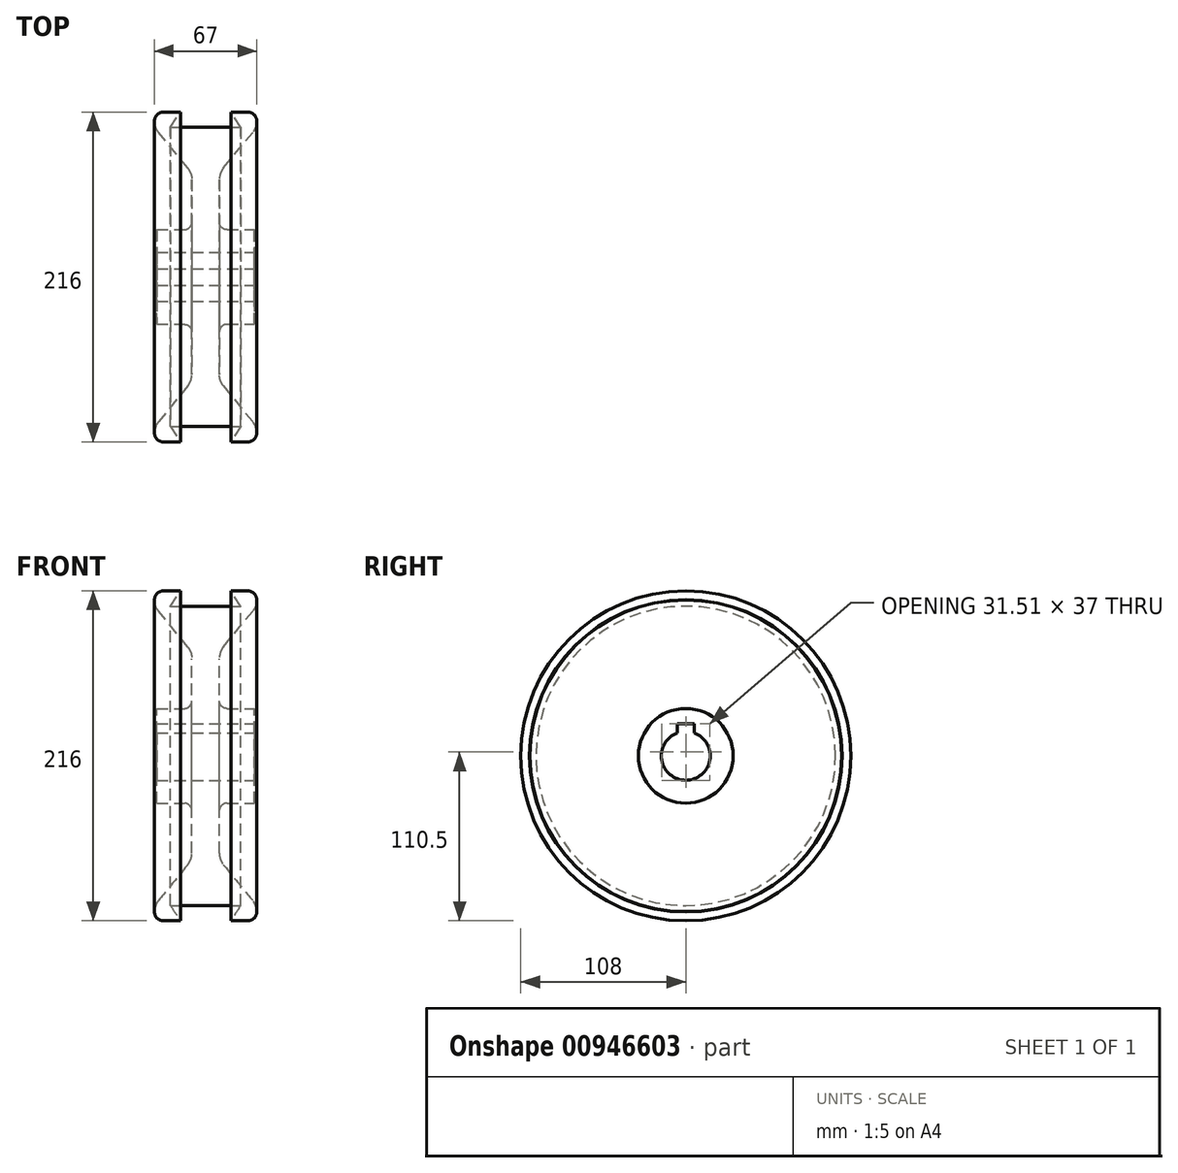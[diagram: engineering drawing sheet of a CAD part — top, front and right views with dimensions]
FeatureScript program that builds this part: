
annotation { "Feature Type Name" : "Feature", "Feature Type Description" : "" }
export const myFeature = defineFeature(function(context is Context, id is Id, definition is map)
    precondition{}
    {
        {
            var Q0;
            Q0=qCreatedBy(makeId("Front.planeOp"),FACE);
            var sketch = newSketch(context, id + "F0", { "sketchPlane" : qUnion([Q0])});
            skLineSegment(sketch, "E0", {"start": v(32, 0) * mm, "end": v(32, 31) * mm});
            skLineSegment(sketch, "E1", {"start": v(32, 31) * mm, "end": v(14, 31) * mm});
            skLineSegment(sketch, "E2", {"start": v(9, 36) * mm, "end": v(9, 63.72) * mm});
            skLineSegment(sketch, "E3", {"start": v(11.7, 71.31) * mm, "end": v(30.8, 94.69) * mm});
            skLineSegment(sketch, "E4", {"start": v(33.5, 102) * mm, "end": v(33.5, 102.28) * mm});
            skLineSegment(sketch, "E5", {"start": v(27.5, 108) * mm, "end": v(16.5, 108) * mm});
            skLineSegment(sketch, "E6", {"start": v(16.5, 108) * mm, "end": v(23, 98) * mm});
            skLineSegment(sketch, "E7", {"start": v(23, 98) * mm, "end": v(0, 98) * mm});
            skLineSegment(sketch, "E8", {"start": v(32, 0) * mm, "end": v(0, 0) * mm});
            skLineSegment(sketch, "E9.MirrorCS", {"start": v(-23, 98) * mm, "end": v(0, 98) * mm});
            skLineSegment(sketch, "E10.MirrorCS", {"start": v(-16.5, 108) * mm, "end": v(-23, 98) * mm});
            skLineSegment(sketch, "E11.MirrorCS", {"start": v(-27.5, 108) * mm, "end": v(-16.5, 108) * mm});
            skLineSegment(sketch, "E12.MirrorCS", {"start": v(-33.5, 102) * mm, "end": v(-33.5, 102.28) * mm});
            skLineSegment(sketch, "E13.MirrorCS", {"start": v(-11.7, 71.31) * mm, "end": v(-30.8, 94.69) * mm});
            skLineSegment(sketch, "E14.MirrorCS", {"start": v(-9, 36) * mm, "end": v(-9, 63.72) * mm});
            skLineSegment(sketch, "E15.MirrorCS", {"start": v(-32, 31) * mm, "end": v(-14, 31) * mm});
            skLineSegment(sketch, "E16.MirrorCS", {"start": v(-32, 0) * mm, "end": v(-32, 31) * mm});
            skLineSegment(sketch, "E17.MirrorCS", {"start": v(-32, 0) * mm, "end": v(0, 0) * mm});
            skPoint(sketch, "E18.visualSharp", {"position": v(-33.5, 108) * mm});
            skArc(sketch, "E18.filletArc", {"start": v(-27.5, 108) * mm, "mid": v(-31.74, 106.24) * mm, "end": v(-33.5, 102) * mm});
            skPoint(sketch, "E19.visualSharp", {"position": v(-33.5, 98) * mm});
            skArc(sketch, "E19.filletArc", {"start": v(-33.5, 102.28) * mm, "mid": v(-32.8, 98.25) * mm, "end": v(-30.8, 94.69) * mm});
            skPoint(sketch, "E20.visualSharp", {"position": v(33.5, 98) * mm});
            skArc(sketch, "E20.filletArc", {"start": v(30.8, 94.69) * mm, "mid": v(32.8, 98.25) * mm, "end": v(33.5, 102.28) * mm});
            skPoint(sketch, "E21.visualSharp", {"position": v(-9, 68) * mm});
            skArc(sketch, "E21.filletArc", {"start": v(-9, 63.72) * mm, "mid": v(-9.7, 67.75) * mm, "end": v(-11.7, 71.31) * mm});
            skPoint(sketch, "E22.visualSharp", {"position": v(9, 68) * mm});
            skArc(sketch, "E22.filletArc", {"start": v(11.7, 71.31) * mm, "mid": v(9.7, 67.75) * mm, "end": v(9, 63.72) * mm});
            skPoint(sketch, "E23.visualSharp", {"position": v(-9, 31) * mm});
            skArc(sketch, "E23.filletArc", {"start": v(-14, 31) * mm, "mid": v(-10.46, 32.46) * mm, "end": v(-9, 36) * mm});
            skPoint(sketch, "E24.visualSharp", {"position": v(9, 31) * mm});
            skArc(sketch, "E24.filletArc", {"start": v(9, 36) * mm, "mid": v(10.46, 32.46) * mm, "end": v(14, 31) * mm});
            skPoint(sketch, "E25.visualSharp", {"position": v(33.5, 108) * mm});
            skArc(sketch, "E25.filletArc", {"start": v(33.5, 102) * mm, "mid": v(31.74, 106.24) * mm, "end": v(27.5, 108) * mm});
            skSolve(sketch);
        }
        {
            var Q0;
            Q0 = qSketchRegion(id + "F0", true);
            var Q1;
            Q1=sQuery(id+"F0.wireOp",EDGE,"E8");
            revolve(context, id + "F1", {"surfaceOperationType" : NewSurfaceOperationType.NEW, "entities" : qUnion([Q0]), "axis" : qUnion([Q1]), "revolveType" : RevolveType.FULL});
        }
        {
            var Q0;
            Q0=makeQuery(id+"F1.opRevolve","SWEPT_FACE",FACE,{"disambiguationData":[OSD([sQuery(id+"F0.wireOp",EDGE,"E0")])]});
            var sketch = newSketch(context, id + "F2", { "sketchPlane" : qUnion([Q0])});
            skArc(sketch, "E26", {"start": v(-5.5, 15.02) * mm, "mid": v(0, -16) * mm, "end": v(5.5, 15.02) * mm});
            skLineSegment(sketch, "E27", {"start": v(-5.5, 15.02) * mm, "end": v(-5.5, 21) * mm});
            skLineSegment(sketch, "E28", {"start": v(5.5, 15.02) * mm, "end": v(5.5, 21) * mm});
            skLineSegment(sketch, "E29", {"start": v(5.5, 21) * mm, "end": v(-5.5, 21) * mm});
            skSolve(sketch);
        }
        {
            var Q0;
            Q0 = qSketchRegion(id + "F2", true);
            extrude(context, id + "F3", {"entities" : qUnion([Q0]), "operationType" : NewBodyOperationType.REMOVE, "oppositeDirection" : true, "depth" : 65 * mm, "offsetDistance" : 25 * mm});
        }
    });
